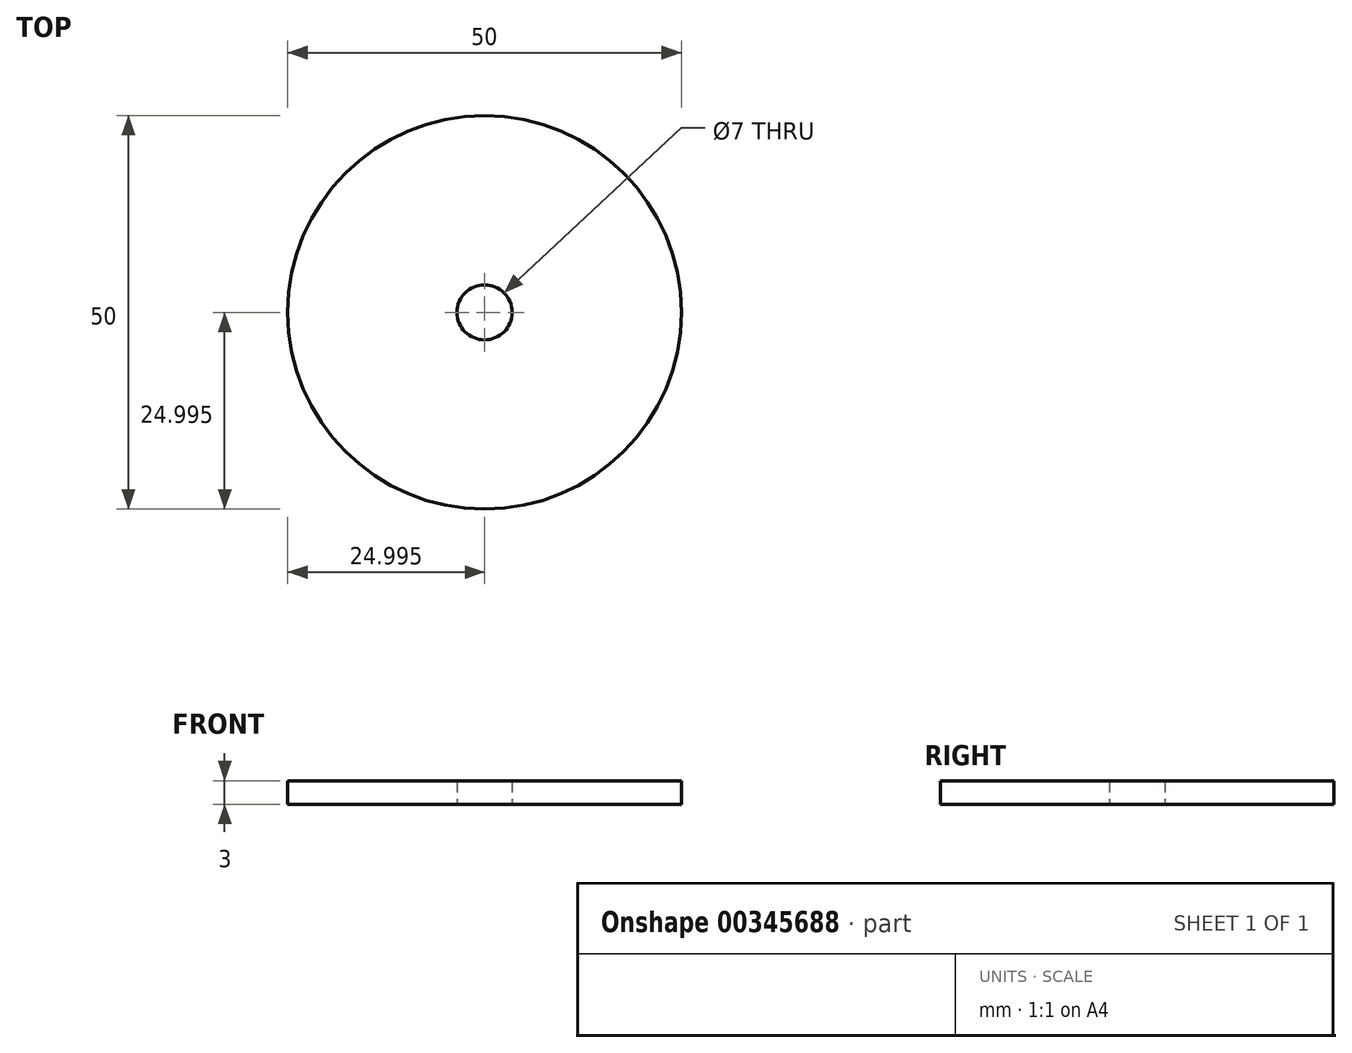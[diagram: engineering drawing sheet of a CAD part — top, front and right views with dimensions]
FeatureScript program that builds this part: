
annotation { "Feature Type Name" : "Feature", "Feature Type Description" : "" }
export const myFeature = defineFeature(function(context is Context, id is Id, definition is map)
    precondition{}
    {
        {
            var Q0;
            Q0=qCreatedBy(makeId("Top.planeOp"),FACE);
            var sketch = newSketch(context, id + "F0", { "sketchPlane" : qUnion([Q0])});
            skCircle(sketch, "E0", {"center": v(-38.31, 8.14) * mm, "radius": 25 * mm});
            skCircle(sketch, "E1", {"center": v(-38.31, 8.14) * mm, "radius": 3.5 * mm});
            skSolve(sketch);
        }
        {
            var Q0;
            Q0=qSketchRegion(id+"F0",true);
            extrude(context, id + "F1", {"entities" : qUnion([Q0]), "depth" : 3 * mm});
        }
    });
